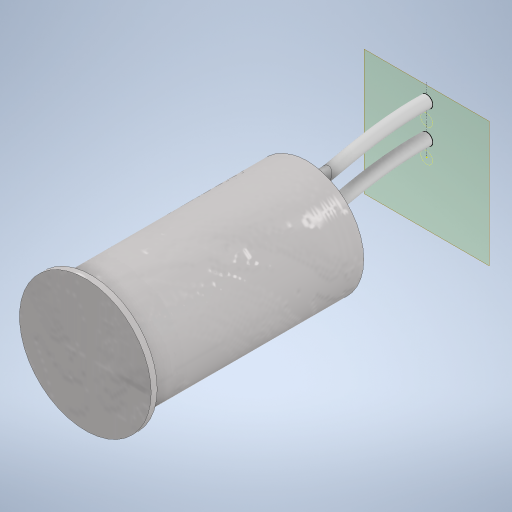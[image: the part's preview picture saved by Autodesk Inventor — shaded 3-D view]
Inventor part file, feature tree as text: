
AUTODESK INVENTOR PART (.ipt)
format: ipt  version: 2024.2 (Build 282272000, 272)  size: 345,600 bytes
history: native  units: mm
features: sketch x5, extrude x2, plane x1, sweep x1, fillet x1
ambient origin geometry x8: Origin, YZ Plane, XZ Plane, XY Plane, X Axis, Y Axis, Z Axis, Center Point
bodies: Solid1 (feature_tree)
feature tree (10):
  extrude  "Extrusion1"  Depth=18.0mm TaperAngle=0.0deg
  extrude  "Extrusion2"  Depth=0.5mm TaperAngle=0.0deg
  sketch  "Sketch3"  dims[d7=1.0mm d8=10.0mm d9=0.0mm d10=0.0mm]
  plane  "Work Plane2"
  sketch  "Sketch4"  dims[d11=1.5mm]
  sweep  "Sweep1"
  fillet  "Fillet1"  [1 undecoded]
  sketch  "Sketch1"  dims[d0=9.5mm d2=18.0mm d3=0.0mm]
  sketch  "Sketch2"  dims[d4=11.0mm d5=0.5mm d6=0.0mm]
  sketch  "Sketch5"
note: 1 required parameter value undecoded (feature->parameter linkage not recoverable at this tier; creation-order binding heuristic only, values carry confidence <= 0.55)
